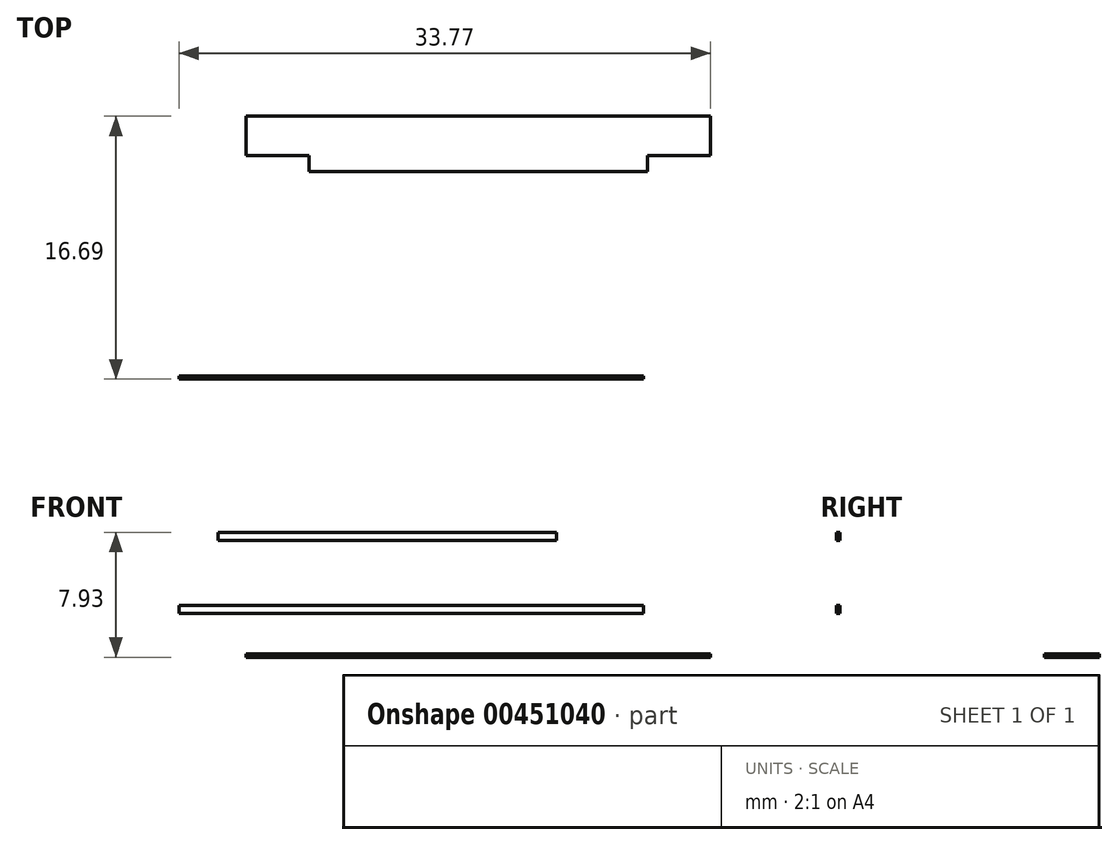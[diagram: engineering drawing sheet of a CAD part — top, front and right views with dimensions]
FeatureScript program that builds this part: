
annotation { "Feature Type Name" : "Feature", "Feature Type Description" : "" }
export const myFeature = defineFeature(function(context is Context, id is Id, definition is map)
    precondition{}
    {
        {
            var Q0;
            Q0=qCreatedBy(makeId("Top.planeOp"),FACE);
            var sketch = newSketch(context, id + "F0", { "sketchPlane" : qUnion([Q0])});
            skLineSegment(sketch, "E0", {"start": v(-34, 16.49) * mm, "end": v(-4.5, 16.49) * mm});
            skLineSegment(sketch, "E1", {"start": v(-4.5, 16.49) * mm, "end": v(-4.5, 13.99) * mm});
            skLineSegment(sketch, "E2", {"start": v(-8.5, 13.99) * mm, "end": v(-4.5, 13.99) * mm});
            skLineSegment(sketch, "E3", {"start": v(-8.5, 13.99) * mm, "end": v(-8.5, 12.99) * mm});
            skLineSegment(sketch, "E4", {"start": v(-8.5, 12.99) * mm, "end": v(-30, 12.99) * mm});
            skLineSegment(sketch, "E5", {"start": v(-30, 12.99) * mm, "end": v(-30, 13.99) * mm});
            skLineSegment(sketch, "E6", {"start": v(-30, 13.99) * mm, "end": v(-34, 13.99) * mm});
            skLineSegment(sketch, "E7", {"start": v(-34, 13.99) * mm, "end": v(-34, 16.49) * mm});
            skSolve(sketch);
        }
        {
            var Q0;
            Q0 = qSketchRegion(id + "F0", true);
            extrude(context, id + "F1", {"entities" : qUnion([Q0]), "depth" : 0.2 * mm});
        }
        {
            var Q0;
            Q0=qCreatedBy(makeId("Front.planeOp"),FACE);
            var sketch = newSketch(context, id + "F2", { "sketchPlane" : qUnion([Q0])});
            skLineSegment(sketch, "E8.bottom", {"start": v(-35.79, 7.93) * mm, "end": v(-14.29, 7.93) * mm});
            skLineSegment(sketch, "E8.top", {"start": v(-35.79, 7.43) * mm, "end": v(-14.29, 7.43) * mm});
            skLineSegment(sketch, "E8.left", {"start": v(-35.79, 7.93) * mm, "end": v(-35.79, 7.43) * mm});
            skLineSegment(sketch, "E8.right", {"start": v(-14.29, 7.93) * mm, "end": v(-14.29, 7.43) * mm});
            skSolve(sketch);
        }
        {
            var Q0;
            Q0 = qSketchRegion(id + "F2", true);
            extrude(context, id + "F3", {"entities" : qUnion([Q0]), "depth" : 0.2 * mm});
        }
        {
            var Q0;
            Q0=qCreatedBy(makeId("Front.planeOp"),FACE);
            var sketch = newSketch(context, id + "F4", { "sketchPlane" : qUnion([Q0])});
            skLineSegment(sketch, "E9.bottom", {"start": v(-38.27, 3.28) * mm, "end": v(-8.77, 3.28) * mm});
            skLineSegment(sketch, "E9.top", {"start": v(-38.27, 2.78) * mm, "end": v(-8.77, 2.78) * mm});
            skLineSegment(sketch, "E9.left", {"start": v(-38.27, 3.28) * mm, "end": v(-38.27, 2.78) * mm});
            skLineSegment(sketch, "E9.right", {"start": v(-8.77, 3.28) * mm, "end": v(-8.77, 2.78) * mm});
            skSolve(sketch);
        }
        {
            var Q0;
            Q0 = qSketchRegion(id + "F4", true);
            extrude(context, id + "F5", {"entities" : qUnion([Q0]), "depth" : 0.2 * mm});
        }
    });
